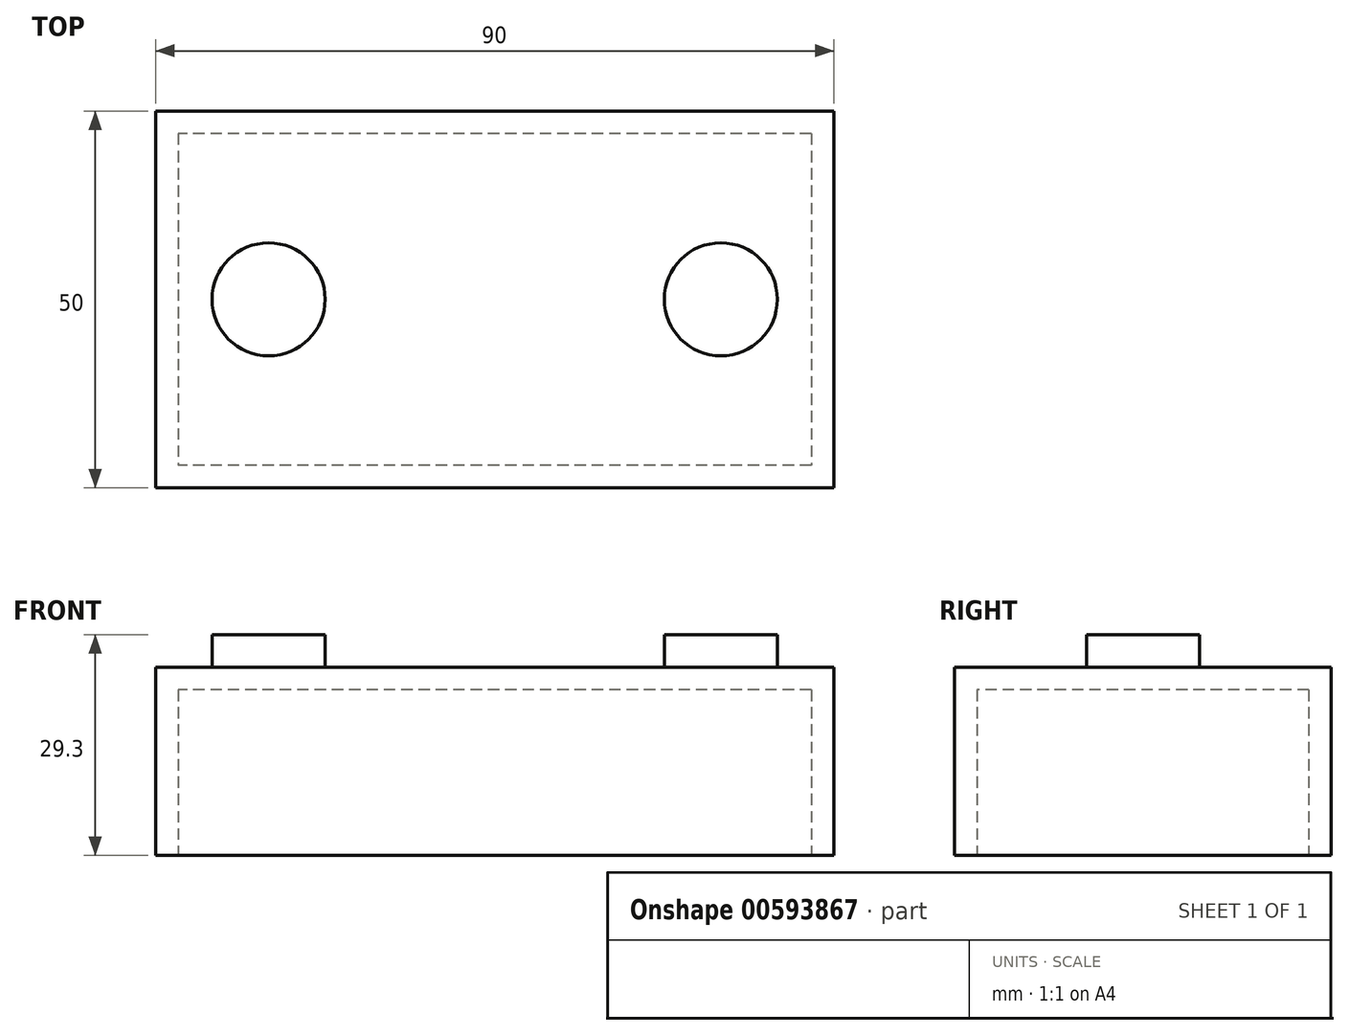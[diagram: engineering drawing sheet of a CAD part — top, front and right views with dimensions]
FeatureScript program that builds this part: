
annotation { "Feature Type Name" : "Feature", "Feature Type Description" : "" }
export const myFeature = defineFeature(function(context is Context, id is Id, definition is map)
    precondition{}
    {
        {
            var Q0;
            Q0=qCreatedBy(makeId("Top.planeOp"),FACE);
            var sketch = newSketch(context, id + "F0", { "sketchPlane" : qUnion([Q0])});
            skLineSegment(sketch, "E0.bottom", {"start": v(45, -25) * mm, "end": v(-45, -25) * mm});
            skLineSegment(sketch, "E0.top", {"start": v(45, 25) * mm, "end": v(-45, 25) * mm});
            skLineSegment(sketch, "E0.left", {"start": v(45, -25) * mm, "end": v(45, 25) * mm});
            skLineSegment(sketch, "E0.right", {"start": v(-45, -25) * mm, "end": v(-45, 25) * mm});
            skLineSegment(sketch, "E1", {"start": v(-45, 25) * mm, "end": v(45, -25) * mm, "construction": true});
            skSolve(sketch);
        }
        {
            var Q0;
            Q0 = qSketchRegion(id + "F0", true);
            extrude(context, id + "F1", {"entities" : qUnion([Q0]), "depth" : 25 * mm, "offsetDistance" : 25 * mm});
        }
        {
            var Q0;
            Q0=makeQuery(id+"F1.opExtrude","CAP_FACE",FACE,{"disambiguationData":[OSD([sQuery(id+"F0.wireOp",EDGE,"E0.bottom"),sQuery(id+"F0.wireOp",EDGE,"E0.top"),sQuery(id+"F0.wireOp",EDGE,"E0.left"),sQuery(id+"F0.wireOp",EDGE,"E0.right")])],"isStart":false});
            var sketch = newSketch(context, id + "F2", { "sketchPlane" : qUnion([Q0])});
            skLineSegment(sketch, "E2", {"start": v(45, 0) * mm, "end": v(-45, 0) * mm, "construction": true});
            skLineSegment(sketch, "E3.1.0.0", {"start": v(30, -25) * mm, "end": v(30, 25) * mm, "construction": true});
            skLineSegment(sketch, "E4.MirrorCS", {"start": v(-30, -25) * mm, "end": v(-30, 25) * mm, "construction": true});
            skCircle(sketch, "E5", {"center": v(30, 0) * mm, "radius": 7.5 * mm});
            skPoint(sketch, "E6.endSnap0", {"position": v(-3.37, -16.33) * mm});
            skCircle(sketch, "E7.MirrorC", {"center": v(-30, 0) * mm, "radius": 7.5 * mm});
            skLineSegment(sketch, "E8", {"start": v(-30, 0) * mm, "end": v(30, 0) * mm, "construction": true});
            skSolve(sketch);
        }
        {
            var Q0;
            Q0 = qSketchRegion(id + "F2", true);
            extrude(context, id + "F3", {"entities" : qUnion([Q0]), "operationType" : NewBodyOperationType.ADD, "depth" : 4.3 * mm, "offsetDistance" : 25 * mm});
        }
        {
            var Q0;
            Q0=makeQuery(id+"F1.opExtrude","CAP_FACE",FACE,{"disambiguationData":[OSD([sQuery(id+"F0.wireOp",EDGE,"E0.bottom"),sQuery(id+"F0.wireOp",EDGE,"E0.top"),sQuery(id+"F0.wireOp",EDGE,"E0.left"),sQuery(id+"F0.wireOp",EDGE,"E0.right")])],"isStart":true});
            var sketch = newSketch(context, id + "F4", { "sketchPlane" : qUnion([Q0])});
            skLineSegment(sketch, "E9.bottom", {"start": v(42, -22) * mm, "end": v(-42, -22) * mm});
            skLineSegment(sketch, "E9.top", {"start": v(42, 22) * mm, "end": v(-42, 22) * mm});
            skLineSegment(sketch, "E9.left", {"start": v(42, -22) * mm, "end": v(42, 22) * mm});
            skLineSegment(sketch, "E9.right", {"start": v(-42, -22) * mm, "end": v(-42, 22) * mm});
            skLineSegment(sketch, "E10", {"start": v(-42, 22) * mm, "end": v(42, -22) * mm, "construction": true});
            skSolve(sketch);
        }
        {
            var Q0;
            Q0 = qSketchRegion(id + "F4", true);
            extrude(context, id + "F5", {"entities" : qUnion([Q0]), "operationType" : NewBodyOperationType.REMOVE, "oppositeDirection" : true, "depth" : 22 * mm, "offsetDistance" : 25 * mm});
        }
    });
